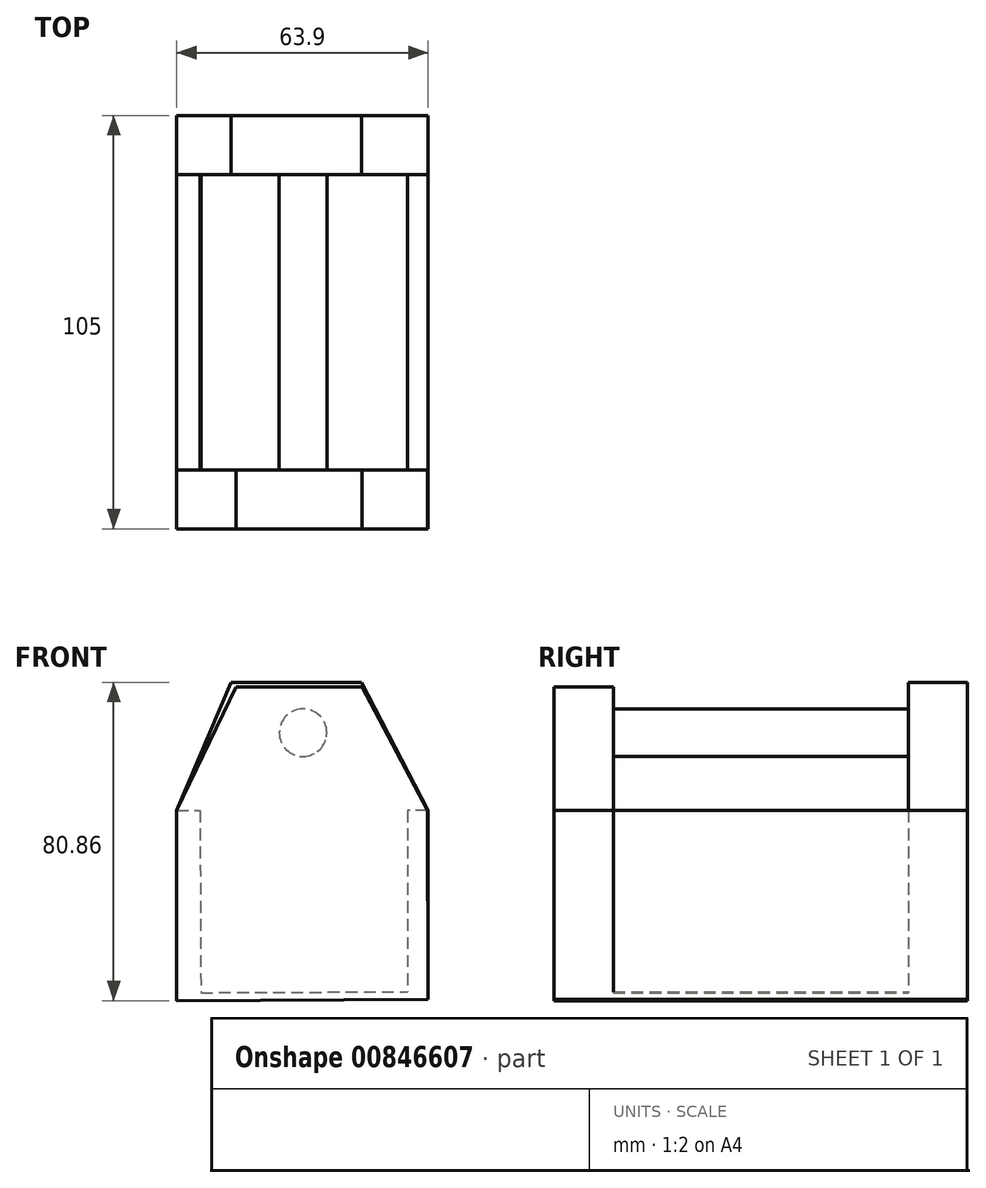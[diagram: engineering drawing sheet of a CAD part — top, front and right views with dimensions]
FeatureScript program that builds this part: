
annotation { "Feature Type Name" : "Feature", "Feature Type Description" : "" }
export const myFeature = defineFeature(function(context is Context, id is Id, definition is map)
    precondition{}
    {
        {
            var Q0;
            Q0=qCreatedBy(makeId("Front.planeOp"),FACE);
            var sketch = newSketch(context, id + "F0", { "sketchPlane" : qUnion([Q0])});
            skLineSegment(sketch, "E0", {"start": v(-18.28, 41.59) * mm, "end": v(14.82, 41.59) * mm});
            skLineSegment(sketch, "E1", {"start": v(14.82, 41.59) * mm, "end": v(31.8, 9.07) * mm});
            skLineSegment(sketch, "E2", {"start": v(31.8, 9.07) * mm, "end": v(31.8, -36.98) * mm});
            skLineSegment(sketch, "E3", {"start": v(-18.28, 41.59) * mm, "end": v(-32.1, 9.07) * mm});
            skLineSegment(sketch, "E4", {"start": v(-32.1, 9.07) * mm, "end": v(-32.1, -37.27) * mm});
            skLineSegment(sketch, "E5", {"start": v(-32.1, -37.27) * mm, "end": v(31.8, -36.98) * mm});
            skSolve(sketch);
        }
        {
            var Q0;
            Q0 = qSketchRegion(id + "F0", true);
            extrude(context, id + "F1", {"entities" : qUnion([Q0]), "depth" : 15 * mm, "offsetDistance" : 25 * mm});
        }
        {
            var Q0;
            Q0=makeQuery(id+"F1.opExtrude","CAP_FACE",FACE,{"disambiguationData":[OSD([sQuery(id+"F0.wireOp",EDGE,"E0"),sQuery(id+"F0.wireOp",EDGE,"E1"),sQuery(id+"F0.wireOp",EDGE,"E2"),sQuery(id+"F0.wireOp",EDGE,"E3"),sQuery(id+"F0.wireOp",EDGE,"E4"),sQuery(id+"F0.wireOp",EDGE,"E5")])],"isStart":false});
            var sketch = newSketch(context, id + "F2", { "sketchPlane" : qUnion([Q0])});
            skLineSegment(sketch, "E6", {"start": v(-32.1, 9.07) * mm, "end": v(-26.16, 9.07) * mm});
            skLineSegment(sketch, "E7", {"start": v(-26.16, 9.07) * mm, "end": v(-25.95, -37.24) * mm});
            skLineSegment(sketch, "E8", {"start": v(-25.95, -37.24) * mm, "end": v(-32.1, -37.27) * mm});
            skLineSegment(sketch, "E9", {"start": v(-32.1, -37.27) * mm, "end": v(-32.1, 9.07) * mm});
            skLineSegment(sketch, "E10", {"start": v(31.8, 9.07) * mm, "end": v(26.49, 9.07) * mm});
            skLineSegment(sketch, "E11", {"start": v(26.49, 9.07) * mm, "end": v(26.49, -37.27) * mm});
            skLineSegment(sketch, "E12", {"start": v(26.49, -37.27) * mm, "end": v(31.8, -36.98) * mm});
            skLineSegment(sketch, "E13", {"start": v(31.8, -36.98) * mm, "end": v(31.8, 9.07) * mm});
            skSolve(sketch);
        }
        {
            var Q0;
            Q0 = qSketchRegion(id + "F2", true);
            extrude(context, id + "F3", {"entities" : qUnion([Q0]), "operationType" : NewBodyOperationType.ADD, "depth" : 75 * mm, "offsetDistance" : 25 * mm});
        }
        {
            var Q0;
            Q0=makeQuery(id+"F3.opExtrude","CAP_FACE",FACE,{"disambiguationData":[OSD([sQuery(id+"F2.wireOp",EDGE,"E6"),sQuery(id+"F2.wireOp",EDGE,"E7"),sQuery(id+"F2.wireOp",EDGE,"E8"),sQuery(id+"F2.wireOp",EDGE,"E9")])],"isStart":false});
            var sketch = newSketch(context, id + "F4", { "sketchPlane" : qUnion([Q0])});
            skLineSegment(sketch, "E14", {"start": v(-32.1, -37.27) * mm, "end": v(31.8, -36.98) * mm});
            skLineSegment(sketch, "E15", {"start": v(31.8, -36.98) * mm, "end": v(31.6, 9.07) * mm});
            skLineSegment(sketch, "E16", {"start": v(31.6, 9.07) * mm, "end": v(15.05, 40.4) * mm});
            skLineSegment(sketch, "E17", {"start": v(15.05, 40.4) * mm, "end": v(-16.96, 40.4) * mm});
            skLineSegment(sketch, "E18", {"start": v(-16.96, 40.4) * mm, "end": v(-32.1, 9.07) * mm});
            skLineSegment(sketch, "E19", {"start": v(-32.1, 9.07) * mm, "end": v(-32.1, -37.27) * mm});
            skSolve(sketch);
        }
        {
            var Q0;
            Q0 = qSketchRegion(id + "F4", true);
            extrude(context, id + "F5", {"entities" : qUnion([Q0]), "operationType" : NewBodyOperationType.ADD, "depth" : 15 * mm, "offsetDistance" : 25 * mm});
        }
        {
            var Q0;
            Q0=makeQuery(id+"F5.boolean.opBoolean","MERGE",FACE,{"derivedFrom":[makeQuery(id+"F3.boolean.opBoolean","MERGE",FACE,{"derivedFrom":[makeQuery(id+"F1.opExtrude","SWEPT_FACE",FACE,{"disambiguationData":[OSD([sQuery(id+"F0.wireOp",EDGE,"E5")])]}),makeQuery(id+"F3.opExtrude","SWEPT_FACE",FACE,{"disambiguationData":[OSD([sQuery(id+"F2.wireOp",EDGE,"E8")])]})]}),makeQuery(id+"F5.opExtrude","SWEPT_FACE",FACE,{"disambiguationData":[OSD([sQuery(id+"F4.wireOp",EDGE,"E14")])]})]});
            var sketch = newSketch(context, id + "F6", { "sketchPlane" : qUnion([Q0])});
            skLineSegment(sketch, "E20", {"start": v(-32.26, 105) * mm, "end": v(31.63, 105) * mm});
            skLineSegment(sketch, "E21", {"start": v(31.63, 105) * mm, "end": v(31.64, 0) * mm});
            skLineSegment(sketch, "E22", {"start": v(31.64, 0) * mm, "end": v(-32.26, 0) * mm});
            skLineSegment(sketch, "E23", {"start": v(-32.26, 0) * mm, "end": v(-32.26, 105) * mm});
            skSolve(sketch);
        }
        {
            var Q0;
            Q0 = qSketchRegion(id + "F6", true);
            extrude(context, id + "F7", {"entities" : qUnion([Q0]), "operationType" : NewBodyOperationType.ADD, "depth" : 2 * mm, "offsetDistance" : 25 * mm});
        }
        {
            var Q0;
            Q0=makeQuery(id+"F5.opExtrude","CAP_FACE",FACE,{"disambiguationData":[OSD([sQuery(id+"F4.wireOp",EDGE,"E14"),sQuery(id+"F4.wireOp",EDGE,"E15"),sQuery(id+"F4.wireOp",EDGE,"E16"),sQuery(id+"F4.wireOp",EDGE,"E17"),sQuery(id+"F4.wireOp",EDGE,"E18"),sQuery(id+"F4.wireOp",EDGE,"E19")])],"isStart":true});
            var sketch = newSketch(context, id + "F8", { "sketchPlane" : qUnion([Q0])});
            skCircle(sketch, "E24", {"center": v(0, 28.8) * mm, "radius": 6.04 * mm});
            skSolve(sketch);
        }
        {
            var Q0;
            Q0 = qSketchRegion(id + "F8", true);
            extrude(context, id + "F9", {"entities" : qUnion([Q0]), "operationType" : NewBodyOperationType.ADD, "depth" : 75 * mm, "offsetDistance" : 25 * mm});
        }
    });
